# Revit family: Drinking_Fountain-Wall_Mounted-Murdock_A171408S-FG-VR-BF1S
name_source: partatom
category: Plumbing Fixtures
units: mm (PartAtom-declared; Revit-internal decimal feet)

## family parameters
Cut with Voids When Loaded = No
Host = Face
OmniClass Number = 23.65.70.14.11
OmniClass Title = Drinking Fountains/Coolers
Part Type = Normal
Room Calculation Point = No
Round Connector Dimension = Use Diameter
Shared = Yes

## types (1)
- A171408S-FG-VR-BF1S
    A171408S-FG-VR-BF - Water cooler = Yes
    ADA Compliant = Yes
    Assembly Code = D2010800
    BF1S = BF1S
    BF1S - Bottle Filler = Yes
    CSC2 - Concealed support carrier = No
    CW Connection = Yes
    CWFU = 1
    Cold Water Connection Diameter = 3/8"
    Cold Water Connection Height = 22 1/4"
    Cold Water Connection Radius = 3/16"
    Cold Water Connection Width = 6 1/2"
    Default Elevation = 0"
    Description = 14GA Stainless Steel, Vandal-Resistant, Wall-Mounted Drinking Fountain with [Heavy-Duty?] Water Bottle Filling Station - Non-Refrigerated, ADA
    Elevation from the Floor Level = 33 1/2"
    Finish = Stainless Steel-Murdock-Polished
    Finish BF1S = Metal-Murdock-Stainless Steel
    Finish Bubler = Stainless Steel-Murdock-Polished
    Finish Push Button = Brass-Murdock-Chrome Plated
    Flow Rate = 1 GPM
    HW Connection = No
    HWFU = 0
    Height = 35 5/8"
    IAPMO Compliance = ANSI A117.1, Public Law 111-380 , (NO-LEAD) CHSC 116875 and Section 9. Fixture meets ADA, ADA Standing Person, and ADA Child requirements when mounted appropriately. NSF/ANSI 61,
    Installation Type = Wall-Mounted
    Length = 18 1/2"
    Manufacturer = Murdock Mfg.
    Material = Stainless Steel-Murdock-Polished
    Model = A171408S-FG-VR-BF1S
    Price = Prices may vary. Please consult Manufacturer Representative for most up-to-date price list.
    Product Documentation Link = https://www.murdockmfg.com
    Product Page URL = https://www.murdockmfg.com
    URL = https://www.murdockmfg.com
    Vent Connection = No
    WB1 - Wall bezel, stainless steel = No
    WF1 - 1500 gallon capacity, NSF 42+53, 1 micron lead reduction filter = No
    WFU = 1.5
    Waste Connection = Yes
    Waste Connection Diameter = 1 1/4"
    Waste Connection Height = 22 1/4"
    Waste Connection Radius = 5/8"
    Waste Connection Width = 4 1/4"
    Water Cooler = A171.8-FG-VR : A171408S-FG-VR
    Width = 18 3/4"

## geometry (parser evidence)
native form markers: Sweep x8
no freeform markers — native parametric forms only
